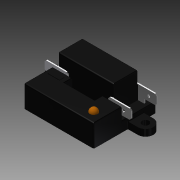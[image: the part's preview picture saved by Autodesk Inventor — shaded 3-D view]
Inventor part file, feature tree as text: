
AUTODESK INVENTOR PART (.ipt)
format: ipt  version: 2014 SP1 (Build 180222100, 222)  size: 414,208 bytes
history: native  units: mm (DEFAULTED — no unit token found)
features: sketch x3, fillet x2, plane x2, extrude x2, other x1, hole x1, mirror x1, imported_body x1
ambient origin geometry x8: Origin, YZ Plane, XZ Plane, XY Plane, X Axis, Y Axis, Z Axis, Center Point
bodies: Solid1 (feature_tree)
feature tree (13):
  other  "Spike Relay.ipt"
  fillet  "Fillet1"  Radius=0.762mm
  sketch  "Sketch2"  dims[d14=13.208mm d15=29.083mm]
  plane  "Work Plane1"
  extrude  "Extrusion1"  Depth=29.083mm
  extrude  "Extrusion2"  Depth=25.4mm TaperAngle=0.0deg
  hole  "Hole1"  [1 undecoded]
  plane  "Work Plane2"
  mirror  "Mirror2"
  fillet  "Fillet2"  [1 undecoded]
  imported_body  "DerivedBody::Spike Relay.ipt"
  sketch  "Sketch3"  dims[d16=34.0868mm d17=-4.318mm d18=25.4mm d19=0.0mm]
  sketch  "Sketch4"  dims[d20=25.4mm d21=0.0mm d22=4.4958mm d23=19.05mm d24=8.4328mm d25=6.35mm d26=14.3117mm d27=25.4mm d28=20.594885mm d29=0.635mm]
note: 2 required parameter values undecoded (feature->parameter linkage not recoverable at this tier; creation-order binding heuristic only, values carry confidence <= 0.55)
